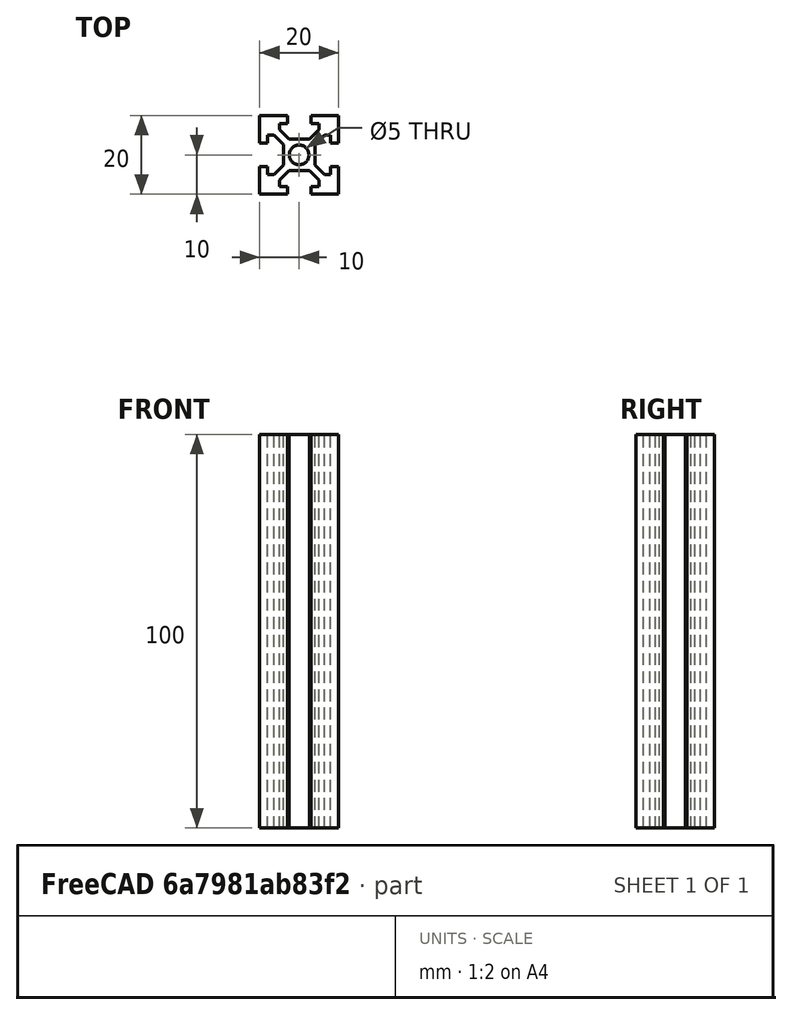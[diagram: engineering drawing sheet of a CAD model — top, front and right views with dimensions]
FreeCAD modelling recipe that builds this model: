
FCSTD DOCUMENT  (FreeCAD 0.19R24276 (Git))
Label: AL_profil_20_L100
License: All rights reserved
LicenseURL: http://en.wikipedia.org/wiki/All_rights_reserved
objects: Sketcher::SketchObject×1, PartDesign::Pad×1, PartDesign::Body×1
note: 4 computed .brp shape members not serialized (recipe doc carries the construction recipe); baked Part::Feature solids carry a one-line shape summary decoded from their .brp

FEATURE [Sketcher::SketchObject] Sketch
  FullyConstrained = false
  MapMode = 5
  Support = -> [XY_Plane]
  sketch-geometry (106):
    g0: LineSegment StartX=10 StartY=10 StartZ=0 EndX=-10 EndY=10 EndZ=0
    g1: LineSegment StartX=-10 StartY=10 StartZ=0 EndX=-10 EndY=-10 EndZ=0
    g2: LineSegment StartX=-10 StartY=-10 StartZ=0 EndX=10 EndY=-10 EndZ=0
    g3: LineSegment StartX=10 StartY=-10 StartZ=0 EndX=10 EndY=10 EndZ=0
    g4: Circle CenterX=0 CenterY=0 CenterZ=0 NormalX=0 NormalY=0 NormalZ=1 AngleXU=0 Radius=14.1421
    g5: LineSegment StartX=4 StartY=4 StartZ=0 EndX=-4 EndY=4 EndZ=0
    g6: LineSegment StartX=-4 StartY=4 StartZ=0 EndX=-4 EndY=-4 EndZ=0
    g7: LineSegment StartX=-4 StartY=-4 StartZ=0 EndX=4 EndY=-4 EndZ=0
    g8: LineSegment StartX=4 StartY=-4 StartZ=0 EndX=4 EndY=4 EndZ=0
    g9: Circle CenterX=0 CenterY=0 CenterZ=0 NormalX=0 NormalY=0 NormalZ=1 AngleXU=0 Radius=5.65685
    g10: Circle CenterX=0 CenterY=0 CenterZ=0 NormalX=0 NormalY=0 NormalZ=1 AngleXU=0 Radius=2.5
    g11: LineSegment StartX=-10 StartY=-10 StartZ=0 EndX=-5 EndY=-10 EndZ=0
    g12: LineSegment StartX=-5 StartY=-10 StartZ=0 EndX=-5 EndY=-5 EndZ=0
    g13: LineSegment StartX=-5 StartY=-5 StartZ=0 EndX=-10 EndY=-5 EndZ=0
    g14: LineSegment StartX=-10 StartY=-5 StartZ=0 EndX=-10 EndY=-10 EndZ=0
    g15: LineSegment StartX=10 StartY=-10 StartZ=0 EndX=5 EndY=-10 EndZ=0
    g16: LineSegment StartX=5 StartY=-8 StartZ=0 EndX=5 EndY=-5 EndZ=0
    g17: LineSegment StartX=5 StartY=-5 StartZ=0 EndX=10 EndY=-5 EndZ=0
    g18: LineSegment StartX=10 StartY=-5 StartZ=0 EndX=10 EndY=-10 EndZ=0
    g19: LineSegment StartX=10 StartY=10 StartZ=0 EndX=5 EndY=10 EndZ=0
    g20: LineSegment StartX=5 StartY=10 StartZ=0 EndX=5 EndY=5 EndZ=0
    g21: LineSegment StartX=5 StartY=5 StartZ=0 EndX=10 EndY=5 EndZ=0
    g22: LineSegment StartX=10 StartY=5 StartZ=0 EndX=10 EndY=10 EndZ=0
    g23: LineSegment StartX=-10 StartY=10 StartZ=0 EndX=-5 EndY=10 EndZ=0
    g24: LineSegment StartX=-5 StartY=10 StartZ=0 EndX=-5 EndY=5 EndZ=0
    g25: LineSegment StartX=-5 StartY=5 StartZ=0 EndX=-10 EndY=5 EndZ=0
    g26: LineSegment StartX=-10 StartY=5 StartZ=0 EndX=-10 EndY=10 EndZ=0
    g27: LineSegment StartX=-6.41421 StartY=-5 StartZ=0 EndX=-4 EndY=-2.58579 EndZ=0
    g28: LineSegment StartX=-5 StartY=-6.41421 StartZ=0 EndX=-2.58579 EndY=-4 EndZ=0
    g29: LineSegment StartX=-5 StartY=-5 StartZ=0 EndX=-4 EndY=-4 EndZ=0
    g30: LineSegment StartX=-4 StartY=-4 StartZ=0 EndX=-5.70711 EndY=-5.70711 EndZ=0
    g31: LineSegment StartX=-6.41421 StartY=5 StartZ=0 EndX=-4 EndY=2.58579 EndZ=0
    g32: LineSegment StartX=-5 StartY=6.41421 StartZ=0 EndX=-2.58579 EndY=4 EndZ=0
    g33: LineSegment StartX=-5 StartY=5 StartZ=0 EndX=-4 EndY=4 EndZ=0
    g34: LineSegment StartX=-4 StartY=4 StartZ=0 EndX=-5.70711 EndY=5.70711 EndZ=0
    g35: LineSegment StartX=6.41421 StartY=-5 StartZ=0 EndX=4 EndY=-2.58579 EndZ=0
    g36: LineSegment StartX=5 StartY=-6.41421 StartZ=0 EndX=2.58579 EndY=-4 EndZ=0
    g37: LineSegment StartX=5 StartY=-5 StartZ=0 EndX=4 EndY=-4 EndZ=0
    g38: LineSegment StartX=4 StartY=-4 StartZ=0 EndX=5.70711 EndY=-5.70711 EndZ=0
    g39: LineSegment StartX=6.41421 StartY=5 StartZ=0 EndX=4 EndY=2.58579 EndZ=0
    g40: LineSegment StartX=5 StartY=6.41421 StartZ=0 EndX=2.58579 EndY=4 EndZ=0
    g41: LineSegment StartX=5 StartY=5 StartZ=0 EndX=4 EndY=4 EndZ=0
    g42: LineSegment StartX=4 StartY=4 StartZ=0 EndX=5.70711 EndY=5.70711 EndZ=0
    g43: LineSegment StartX=10 StartY=-10 StartZ=0 EndX=3 EndY=-10 EndZ=0
    g44: LineSegment StartX=3 StartY=-10 StartZ=0 EndX=3 EndY=-8 EndZ=0
    g45: LineSegment StartX=3 StartY=-8 StartZ=0 EndX=5 EndY=-8 EndZ=0
    g46: LineSegment StartX=10 StartY=-8 StartZ=0 EndX=10 EndY=-10 EndZ=0
    g47: LineSegment StartX=10 StartY=-3 StartZ=0 EndX=8 EndY=-3 EndZ=0
    g48: LineSegment StartX=8 StartY=-3 StartZ=0 EndX=8 EndY=-5 EndZ=0
    g49: LineSegment StartX=3 StartY=-10 StartZ=0 EndX=3 EndY=-8 EndZ=0
    g50: LineSegment StartX=3 StartY=-8 StartZ=0 EndX=5 EndY=-8 EndZ=0
    g51: LineSegment StartX=5 StartY=-8 StartZ=0 EndX=5 EndY=-6.41421 EndZ=0
    g52: LineSegment StartX=5 StartY=-6.41421 StartZ=0 EndX=2.58579 EndY=-4 EndZ=0
    g53: LineSegment StartX=4 StartY=-2.58579 StartZ=0 EndX=6.41421 EndY=-5 EndZ=0
    g54: LineSegment StartX=6.41421 StartY=-5 StartZ=0 EndX=8 EndY=-5 EndZ=0
    g55: LineSegment StartX=8 StartY=-5 StartZ=0 EndX=8 EndY=-3 EndZ=0
    g56: LineSegment StartX=8 StartY=-3 StartZ=0 EndX=10 EndY=-3 EndZ=0
    g57: LineSegment StartX=-2.58579 StartY=-4 StartZ=0 EndX=2.58579 EndY=-4 EndZ=0
    g58: LineSegment StartX=3 StartY=10 StartZ=0 EndX=3 EndY=8 EndZ=0
    g59: LineSegment StartX=3 StartY=8 StartZ=0 EndX=5 EndY=8 EndZ=0
    g60: LineSegment StartX=3 StartY=10 StartZ=0 EndX=3 EndY=8 EndZ=0
    g61: LineSegment StartX=3 StartY=8 StartZ=0 EndX=5 EndY=8 EndZ=0
    g62: LineSegment StartX=10 StartY=3 StartZ=0 EndX=8 EndY=3 EndZ=0
    g63: LineSegment StartX=8 StartY=3 StartZ=0 EndX=8 EndY=5 EndZ=0
    g64: LineSegment StartX=8 StartY=5 StartZ=0 EndX=8 EndY=3 EndZ=0
    g65: LineSegment StartX=8 StartY=3 StartZ=0 EndX=10 EndY=3 EndZ=0
    g66: LineSegment StartX=2.58579 StartY=4 StartZ=0 EndX=5 EndY=6.41421 EndZ=0
    g67: LineSegment StartX=5 StartY=6.41421 StartZ=0 EndX=5 EndY=8 EndZ=0
    g68: LineSegment StartX=-2.58579 StartY=4 StartZ=0 EndX=2.58579 EndY=4 EndZ=0
    g69: LineSegment StartX=4 StartY=2.58579 StartZ=0 EndX=6.41421 EndY=5 EndZ=0
    g70: LineSegment StartX=6.41421 StartY=5 StartZ=0 EndX=8 EndY=5 EndZ=0
    g71: LineSegment StartX=4 StartY=-2.58579 StartZ=0 EndX=4 EndY=2.58579 EndZ=0
    g72: LineSegment StartX=10 StartY=3 StartZ=0 EndX=10 EndY=10 EndZ=0
    g73: LineSegment StartX=10 StartY=-10 StartZ=0 EndX=10 EndY=-3 EndZ=0
    g74: LineSegment StartX=-3 StartY=-10 StartZ=0 EndX=-3 EndY=-8 EndZ=0
    g75: LineSegment StartX=-3 StartY=-8 StartZ=0 EndX=-5 EndY=-8 EndZ=0
    g76: LineSegment StartX=-3 StartY=-10 StartZ=0 EndX=-3 EndY=-8 EndZ=0
    g77: LineSegment StartX=-3 StartY=-8 StartZ=0 EndX=-5 EndY=-8 EndZ=0
    g78: LineSegment StartX=-5 StartY=-8 StartZ=0 EndX=-5 EndY=-6.41421 EndZ=0
    g79: LineSegment StartX=-10 StartY=-3 StartZ=0 EndX=-8 EndY=-3 EndZ=0
    g80: LineSegment StartX=-8 StartY=-3 StartZ=0 EndX=-8 EndY=-5 EndZ=0
    g81: LineSegment StartX=-6.41421 StartY=-5 StartZ=0 EndX=-8 EndY=-5 EndZ=0
    g82: LineSegment StartX=-8 StartY=-5 StartZ=0 EndX=-8 EndY=-3 EndZ=0
    g83: LineSegment StartX=-8 StartY=-3 StartZ=0 EndX=-10 EndY=-3 EndZ=0
    g84: LineSegment StartX=-10 StartY=10 StartZ=0 EndX=10 EndY=10 EndZ=0
    g85: LineSegment StartX=-6.41421 StartY=-5 StartZ=0 EndX=-4 EndY=-2.58579 EndZ=0
    g86: LineSegment StartX=-4 StartY=2.58579 StartZ=0 EndX=-4 EndY=-2.58579 EndZ=0
    g87: LineSegment StartX=-5 StartY=-6.41421 StartZ=0 EndX=-2.58579 EndY=-4 EndZ=0
    g88: LineSegment StartX=3 StartY=-10 StartZ=0 EndX=10 EndY=-10 EndZ=0
    g89: LineSegment StartX=-3 StartY=-10 StartZ=0 EndX=-10 EndY=-10 EndZ=0
    g90: LineSegment StartX=-10 StartY=3 StartZ=0 EndX=-8 EndY=3 EndZ=0
    g91: LineSegment StartX=-8 StartY=3 StartZ=0 EndX=-8 EndY=5 EndZ=0
    g92: LineSegment StartX=-8 StartY=5 StartZ=0 EndX=-8 EndY=3 EndZ=0
    g93: LineSegment StartX=-8 StartY=3 StartZ=0 EndX=-10 EndY=3 EndZ=0
    g94: LineSegment StartX=-3 StartY=10 StartZ=0 EndX=-3 EndY=8 EndZ=0
    g95: LineSegment StartX=-3 StartY=8 StartZ=0 EndX=-5 EndY=8 EndZ=0
    g96: LineSegment StartX=-3 StartY=10 StartZ=0 EndX=-3 EndY=8 EndZ=0
    g97: LineSegment StartX=-3 StartY=8 StartZ=0 EndX=-5 EndY=8 EndZ=0
    g98: LineSegment StartX=-5 StartY=8 StartZ=0 EndX=-5 EndY=6.41421 EndZ=0
    g99: LineSegment StartX=-6.41421 StartY=5 StartZ=0 EndX=-8 EndY=5 EndZ=0
    g100: LineSegment StartX=-5 StartY=6.41421 StartZ=0 EndX=-2.58579 EndY=4 EndZ=0
    g101: LineSegment StartX=-6.41421 StartY=5 StartZ=0 EndX=-4 EndY=2.58579 EndZ=0
    g102: LineSegment StartX=-10 StartY=-3 StartZ=0 EndX=-10 EndY=-10 EndZ=0
    g103: LineSegment StartX=-10 StartY=3 StartZ=0 EndX=-10 EndY=10 EndZ=0
    g104: LineSegment StartX=-10 StartY=10 StartZ=0 EndX=-3 EndY=10 EndZ=0
    g105: LineSegment StartX=3 StartY=10 StartZ=0 EndX=10 EndY=10 EndZ=0
  constraints (271):
    c: Coincident(g0,g1)
    c: Coincident(g1,g2)
    c: Coincident(g2,g3)
    c: Coincident(g3,g0)
    c: Equal(g0,g1)
    c: Equal(g0,g2)
    c: Equal(g0,g3)
    c: PointOnObject(g0,g4)
    c: PointOnObject(g1,g4)
    c: PointOnObject(g2,g4)
    c: PointOnObject(g3,g4)
    c: Coincident(g4,g-1)
    c: Horizontal(g0)
    c: Coincident(g5,g6)
    c: Coincident(g6,g7)
    c: Coincident(g7,g8)
    c: Coincident(g8,g5)
    c: Equal(g5,g6)
    c: Equal(g5,g7)
    c: Equal(g5,g8)
    c: PointOnObject(g5,g9)
    c: PointOnObject(g6,g9)
    c: PointOnObject(g7,g9)
    c: PointOnObject(g8,g9)
    c: Coincident(g9,g-1)
    c: Horizontal(g5)
    c: DistanceX(g5,g5) = 8
    c: Diameter(g10) = 5
    c: DistanceX(g2,g2) = 20
    c: Coincident(g10,g-1)
    c: Coincident(g11,g12)
    c: Coincident(g12,g13)
    c: Coincident(g13,g14)
    c: Coincident(g14,g11)
    c: Horizontal(g11)
    c: Horizontal(g13)
    c: Vertical(g12)
    c: Vertical(g14)
    c: Coincident(g11,g1)
    c: Coincident(g16,g17)
    c: Coincident(g17,g18)
    c: Coincident(g18,g15)
    c: Horizontal(g15)
    c: Horizontal(g17)
    c: Vertical(g16)
    c: Vertical(g18)
    c: Coincident(g15,g2)
    c: Coincident(g19,g20)
    c: Coincident(g20,g21)
    c: Coincident(g21,g22)
    c: Coincident(g22,g19)
    c: Horizontal(g19)
    c: Horizontal(g21)
    c: Vertical(g20)
    c: Vertical(g22)
    c: Coincident(g19,g0)
    c: Coincident(g23,g24)
    c: Coincident(g24,g25)
    c: Coincident(g25,g26)
    c: Coincident(g26,g23)
    c: Horizontal(g23)
    c: Horizontal(g25)
    c: Vertical(g24)
    c: Vertical(g26)
    c: Coincident(g23,g0)
    c: DistanceX(g1,g11) = 5
    c: Equal(g12,g13)
    c: Equal(g13,g17)
    c: Equal(g25,g13)
    c: Equal(g13,g21)
    c: Equal(g24,g20)
    c: Equal(g20,g12)
    c: Parallel(g27,g28)
    c: Coincident(g29,g12)
    c: Coincident(g29,g6)
    c: Parallel(g27,g29)
    c: Coincident(g30,g6)
    c: Parallel(g29,g30)
    c: PointOnObject(g28,g12)
    c: PointOnObject(g27,g13)
    c: Distance(g28,g27) = 2
    c: PointOnObject(g27,g6)
    c: PointOnObject(g28,g7)
    c: Symmetric(g27,g28,g30)
    c: Parallel(g31,g32)
    c: Parallel(g31,g33)
    c: Parallel(g33,g34)
    c: Coincident(g33,g34)
    c: Coincident(g33,g5)
    c: Coincident(g33,g24)
    c: PointOnObject(g31,g25)
    c: PointOnObject(g32,g24)
    c: PointOnObject(g32,g5)
    c: PointOnObject(g31,g6)
    c: Symmetric(g31,g32,g34)
    c: Distance(g31,g32) = 2
    c: Parallel(g35,g36)
    c: Parallel(g35,g37)
    c: Parallel(g37,g38)
    c: Parallel(g39,g40)
    c: Parallel(g39,g41)
    c: Parallel(g41,g42)
    c: Coincident(g41,g42)
    c: Coincident(g41,g5)
    c: PointOnObject(g40,g5)
    c: PointOnObject(g39,g8)
    c: PointOnObject(g39,g21)
    c: PointOnObject(g40,g20)
    c: Coincident(g20,g41)
    c: Distance(g40,g39) = 2
    c: Symmetric(g40,g39,g42)
    c: PointOnObject(g35,g8)
    c: PointOnObject(g35,g17)
    c: PointOnObject(g36,g16)
    c: PointOnObject(g36,g7)
    c: Coincident(g38,g37)
    c: Coincident(g38,g7)
    c: Coincident(g37,g16)
    c: Symmetric(g36,g35,g38)
    c: Distance(g36,g35) = 2
    c: Coincident(g43,g44)
    c: Coincident(g44,g45)
    c: Coincident(g46,g43)
    c: Horizontal(g43)
    c: Horizontal(g45)
    c: Vertical(g44)
    c: Vertical(g46)
    c: Coincident(g43,g2)
    c: DistanceX(g43,g2) = 7
    c: DistanceY(g2,g46) = 2
    c: Coincident(g45,g16)
    c: Coincident(g47,g48)
    c: Equal(g44,g47)
    c: Vertical(g48)
    c: Horizontal(g47)
    c: Vertical(g47,g2)
    c: Horizontal(g17,g13)
    c: PointOnObject(g48,g17)
    c: DistanceY(g2,g47) = 7
    c: DistanceX(g47,g47) = 2
    c: Coincident(g49,g43)
    c: Coincident(g50,g44)
    c: Coincident(g51,g50)
    c: Coincident(g52,g51)
    c: Coincident(g53,g35)
    c: Coincident(g54,g53)
    c: Coincident(g55,g48)
    c: Coincident(g56,g55)
    c: Coincident(g49,g50)
    c: Coincident(g50,g16)
    c: Coincident(g51,g36)
    c: Coincident(g52,g36)
    c: Coincident(g53,g35)
    c: Coincident(g54,g55)
    c: Coincident(g55,g47)
    c: Coincident(g56,g47)
    c: Coincident(g57,g28)
    c: Coincident(g57,g52)
    c: Coincident(g58,g59)
    c: Horizontal(g59)
    c: Vertical(g58)
    c: Coincident(g62,g63)
    c: Equal(g58,g62)
    c: Vertical(g63)
    c: Horizontal(g62)
    c: Coincident(g61,g58)
    c: Coincident(g64,g63)
    c: Coincident(g65,g64)
    c: Coincident(g60,g61)
    c: Coincident(g64,g62)
    c: Coincident(g65,g62)
    c: Equal(g56,g65)
    c: Vertical(g65,g56)
    c: Equal(g55,g64)
    c: Horizontal(g64,g21)
    c: Equal(g61,g64)
    c: Horizontal(g60,g19)
    c: Coincident(g60,g58)
    c: Coincident(g61,g59)
    c: Vertical(g61,g19)
    c: Coincident(g66,g40)
    c: Coincident(g67,g66)
    c: Coincident(g67,g61)
    c: Coincident(g66,g40)
    c: Coincident(g68,g32)
    c: Coincident(g68,g66)
    c: Coincident(g69,g39)
    c: Coincident(g70,g69)
    c: Coincident(g69,g39)
    c: Coincident(g70,g64)
    c: Coincident(g71,g53)
    c: Coincident(g71,g69)
    c: Coincident(g72,g65)
    c: Coincident(g72,g0)
    c: Coincident(g73,g2)
    c: Coincident(g73,g56)
    c: Horizontal(g84)
    c: Coincident(g74,g75)
    c: Horizontal(g75)
    c: Vertical(g74)
    c: Coincident(g79,g80)
    c: Equal(g74,g79)
    c: Vertical(g80)
    c: Horizontal(g79)
    c: Coincident(g77,g74)
    c: Coincident(g78,g77)
    c: Coincident(g82,g80)
    c: Coincident(g83,g82)
    c: Coincident(g76,g77)
    c: Coincident(g81,g82)
    c: Coincident(g82,g79)
    c: Coincident(g83,g79)
    c: Horizontal(g76,g49)
    c: Horizontal(g76,g49)
    c: Vertical(g78)
    c: Coincident(g77,g75)
    c: Coincident(g78,g28)
    c: Equal(g77,g50)
    c: Vertical(g83,g1)
    c: Coincident(g74,g76)
    c: Equal(g82,g77)
    c: Horizontal(g81)
    c: Coincident(g81,g27)
    c: Coincident(g85,g81)
    c: Coincident(g85,g27)
    c: Coincident(g86,g31)
    c: Coincident(g86,g85)
    c: Coincident(g87,g78)
    c: Coincident(g87,g57)
    c: Coincident(g88,g49)
    c: Coincident(g89,g76)
    c: Coincident(g1,g89)
    c: Coincident(g88,g73)
    c: Coincident(g94,g95)
    c: Horizontal(g95)
    c: Vertical(g94)
    c: Coincident(g90,g91)
    c: Equal(g94,g90)
    c: Vertical(g91)
    c: Horizontal(g90)
    c: Coincident(g97,g94)
    c: Coincident(g98,g97)
    c: Coincident(g92,g91)
    c: Coincident(g93,g92)
    c: Coincident(g96,g97)
    c: Coincident(g99,g92)
    c: Coincident(g92,g90)
    c: Coincident(g93,g90)
    c: Vertical(g98)
    c: Coincident(g97,g95)
    c: Coincident(g94,g96)
    c: Equal(g92,g97)
    c: Horizontal(g99)
    c: Horizontal(g96,g23)
    c: Equal(g97,g61)
    c: Horizontal(g60,g96)
    c: Coincident(g98,g32)
    c: Coincident(g100,g98)
    c: Coincident(g68,g100)
    c: Coincident(g99,g31)
    c: Vertical(g92,g82)
    c: Coincident(g101,g99)
    c: Coincident(g101,g86)
    c: Coincident(g102,g83)
    c: Coincident(g103,g93)
    c: Coincident(g104,g0)
    c: Coincident(g105,g60)
    c: Coincident(g103,g104)
    c: Coincident(g102,g89)
    c: Coincident(g104,g96)
    c: Coincident(g105,g72)
FEATURE [PartDesign::Pad] Pad
  Direction = (1,1,1)
  Length = 100
  Length2 = 100
  Profile = -> Sketch
  Type = 0
FEATURE [PartDesign::Body] Body
  Group = -> [Sketch,Pad]
  Origin = -> Origin
  Tip = -> Pad
